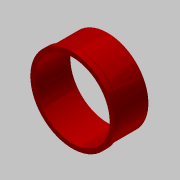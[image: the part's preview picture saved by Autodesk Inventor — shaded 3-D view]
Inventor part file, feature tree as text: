
AUTODESK INVENTOR PART (.ipt)
format: ipt  version: 2017.3 (Build 213257000, 257)  size: 169,472 bytes
history: native  units: in
note: dims shown in document units (in); Inventor stores cm internally (conversion verified against a paired STEP export)
features: extrude x6, sketch x6, chamfer x4, fillet x1, revolve x1
ambient origin geometry x8: Origin, YZ Plane, XZ Plane, XY Plane, X Axis, Y Axis, Z Axis, Center Point
bodies: Solid1 (feature_tree)
feature tree (18):
  extrude  "Extrusion1"  Depth=31.0in
  sketch  "Sketch2"  dims[d2=12.0in d3=0.0in d4=31.23in]
  extrude  "Extrusion2"  Depth=12.0in
  extrude  "Extrusion3"  Depth=1.0in TaperAngle=0.0deg
  chamfer  "Chamfer1"  Distance=1.0in
  extrude  "Extrusion4"  Depth=0.125in TaperAngle=45.0deg
  fillet  "Fillet1"  Radius=29.98in
  chamfer  "Chamfer2"  Distance=0.5in
  chamfer  "Chamfer3"  Distance=0.0312in Angle=45.0deg
  revolve  "Revolution1"  [1 undecoded]
  extrude  "Extrusion7"  Depth=1.0in
  extrude  "Extrusion8"  Depth=1.0in
  chamfer  "Chamfer4"  Distance=1.25in
  sketch  "Sketch1"  dims[d0=28.5in d1=31.0in]
  sketch  "Sketch3"  dims[d5=31.48in d6=2.0in d7=0.0in d8=1.0in d9=0.0in]
  sketch  "Sketch4"  dims[d10=0.115in d11=0.125in d12=45.0deg d13=29.98in d14=0.5in d15=0.0in]
  sketch  "Sketch7"  dims[d16=0.0312in d17=0.0312in d18=0.125in d19=45.0deg]
  sketch  "Sketch8"  dims[d20=0.0312in d21=0.125in d22=45.0deg d23=0.4375in d24=0.125in d25=0.1875in d26=1.25in d27=45.0deg d28=90.0deg d34=1.0in d35=0.0in d36=0.5in d37=2.0in d38=0.0in d39=0.0in d40=0.375in d41=0.125in d42=45.0deg d43=0.25in]
note: 1 required parameter value undecoded (feature->parameter linkage not recoverable at this tier; creation-order binding heuristic only, values carry confidence <= 0.55)
